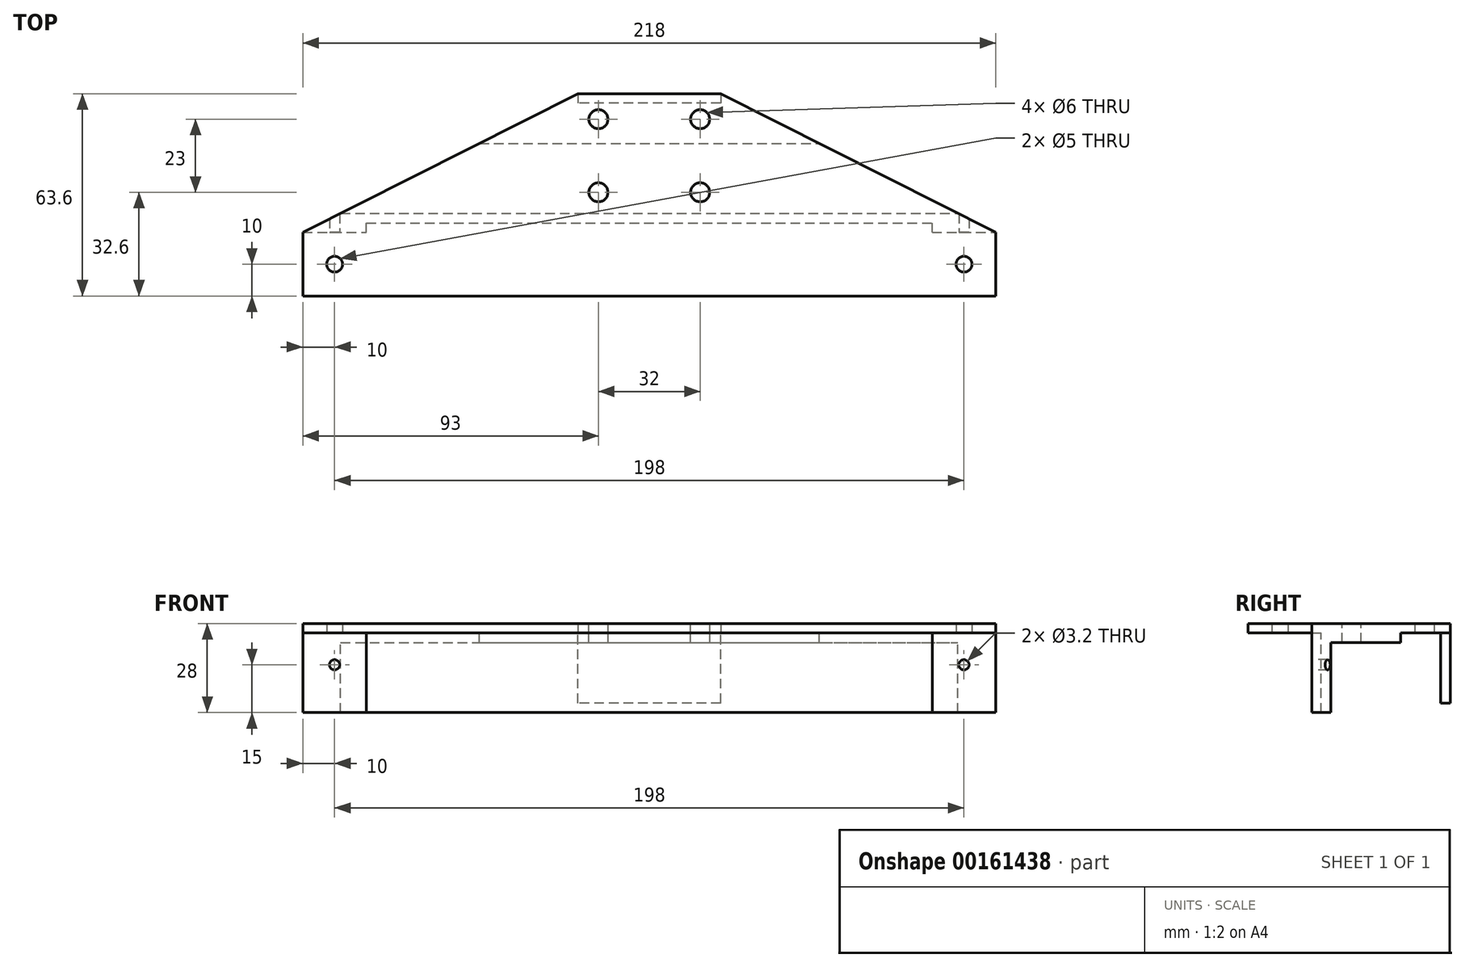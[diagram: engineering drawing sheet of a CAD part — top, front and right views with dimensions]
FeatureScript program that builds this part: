
annotation { "Feature Type Name" : "Feature", "Feature Type Description" : "" }
export const myFeature = defineFeature(function(context is Context, id is Id, definition is map)
    precondition{}
    {
        {
            var Q0;
            Q0=qCreatedBy(makeId("Top.planeOp"),FACE);
            var sketch = newSketch(context, id + "F0", { "sketchPlane" : qUnion([Q0])});
            skLineSegment(sketch, "E0.top", {"start": v(109, -10) * mm, "end": v(-109, -10) * mm});
            skLineSegment(sketch, "E0.left", {"start": v(109, 10) * mm, "end": v(109, -10) * mm});
            skLineSegment(sketch, "E0.right", {"start": v(-109, 10) * mm, "end": v(-109, -10) * mm});
            skLineSegment(sketch, "E1.bottom", {"start": v(22.5, 53.6) * mm, "end": v(-22.5, 53.6) * mm});
            skPoint(sketch, "E1.top.end.orphan", {"position": v(-22.5, -53.6) * mm});
            skPoint(sketch, "E1.top.start.orphan", {"position": v(22.5, -53.6) * mm});
            skLineSegment(sketch, "E2", {"start": v(-109, 10) * mm, "end": v(-22.5, 53.6) * mm});
            skLineSegment(sketch, "E3", {"start": v(22.5, 53.6) * mm, "end": v(109, 10) * mm});
            skPoint(sketch, "E4", {"position": v(-99, 0) * mm});
            skPoint(sketch, "E5", {"position": v(99, 0) * mm});
            skPoint(sketch, "E5.positionSnap0", {"position": v(109, 0) * mm});
            skCircle(sketch, "E6", {"center": v(-99, 0) * mm, "radius": 2.5 * mm});
            skCircle(sketch, "E7", {"center": v(99, 0) * mm, "radius": 2.5 * mm});
            skLineSegment(sketch, "E8.top", {"start": v(3, -10) * mm, "end": v(18, -10) * mm});
            skSolve(sketch);
        }
        {
            var Q0;
            Q0 = qSketchRegion(id + "F0", true);
            extrude(context, id + "F1", {"entities" : qUnion([Q0]), "depth" : 3 * mm});
        }
        {
            var Q0;
            Q0=makeQuery(id+"F1.opExtrude","CAP_FACE",FACE,{"disambiguationData":[OSD([sQuery(id+"F0.wireOp",EDGE,"E0.top"),sQuery(id+"F0.wireOp",EDGE,"E0.left"),sQuery(id+"F0.wireOp",EDGE,"E0.right"),sQuery(id+"F0.wireOp",EDGE,"E1.bottom"),sQuery(id+"F0.wireOp",EDGE,"E2"),sQuery(id+"F0.wireOp",EDGE,"E3"),sQuery(id+"F0.wireOp",EDGE,"E6"),sQuery(id+"F0.wireOp",EDGE,"E7")])],"isStart":true});
            var sketch = newSketch(context, id + "F2", { "sketchPlane" : qUnion([Q0])});
            skLineSegment(sketch, "E9.bottom", {"start": v(22.5, -53.6) * mm, "end": v(-22.5, -53.6) * mm});
            skLineSegment(sketch, "E9.top", {"start": v(22.5, -50.6) * mm, "end": v(-22.5, -50.6) * mm});
            skLineSegment(sketch, "E9.left", {"start": v(22.5, -53.6) * mm, "end": v(22.5, -50.6) * mm});
            skLineSegment(sketch, "E9.right", {"start": v(-22.5, -53.6) * mm, "end": v(-22.5, -50.6) * mm});
            skPoint(sketch, "E10.left.start.orphan", {"position": v(-89, 10) * mm});
            skPoint(sketch, "E10.right.start.orphan", {"position": v(89, 10) * mm});
            skSolve(sketch);
        }
        {
            var Q0;
            Q0 = qSketchRegion(id + "F2", true);
            extrude(context, id + "F3", {"entities" : qUnion([Q0]), "operationType" : NewBodyOperationType.ADD, "depth" : 22 * mm});
        }
        {
            var Q0;
            Q0=makeQuery(id+"F1.opExtrude","CAP_FACE",FACE,{"disambiguationData":[OSD([sQuery(id+"F0.wireOp",EDGE,"E0.top"),sQuery(id+"F0.wireOp",EDGE,"E0.left"),sQuery(id+"F0.wireOp",EDGE,"E0.right"),sQuery(id+"F0.wireOp",EDGE,"E1.bottom"),sQuery(id+"F0.wireOp",EDGE,"E2"),sQuery(id+"F0.wireOp",EDGE,"E3"),sQuery(id+"F0.wireOp",EDGE,"E6"),sQuery(id+"F0.wireOp",EDGE,"E7")])],"isStart":true});
            var sketch = newSketch(context, id + "F4", { "sketchPlane" : qUnion([Q0])});
            skPoint(sketch, "E11.right.end.orphan", {"position": v(109, -35) * mm});
            skLineSegment(sketch, "E12", {"start": v(-89, -13) * mm, "end": v(89, -13) * mm});
            skLineSegment(sketch, "E13", {"start": v(-53.45, -38) * mm, "end": v(53.45, -38) * mm});
            skLineSegment(sketch, "E14", {"start": v(-103.05, -13) * mm, "end": v(-53.45, -38) * mm});
            skLineSegment(sketch, "E15", {"start": v(53.45, -38) * mm, "end": v(103.05, -13) * mm});
            skLineSegment(sketch, "E16", {"start": v(-109, -10) * mm, "end": v(-89, -10) * mm});
            skLineSegment(sketch, "E17", {"start": v(-109, -10) * mm, "end": v(-103.05, -13) * mm});
            skLineSegment(sketch, "E18", {"start": v(109, -10) * mm, "end": v(103.05, -13) * mm});
            skLineSegment(sketch, "E19", {"start": v(89, -10) * mm, "end": v(89, -13) * mm});
            skLineSegment(sketch, "E20", {"start": v(-89, -10) * mm, "end": v(-89, -13) * mm});
            skLineSegment(sketch, "E21.trimOffspring", {"start": v(89, -10) * mm, "end": v(109, -10) * mm});
            skSolve(sketch);
        }
        {
            var Q0;
            Q0 = qSketchRegion(id + "F4", true);
            extrude(context, id + "F5", {"entities" : qUnion([Q0]), "operationType" : NewBodyOperationType.ADD, "depth" : 3 * mm});
        }
        {
            var Q0;
            Q0=makeQuery(id+"F5.opExtrude","CAP_FACE",FACE,{"disambiguationData":[OSD([sQuery(id+"F4.wireOp",EDGE,"E12"),sQuery(id+"F4.wireOp",EDGE,"E13"),sQuery(id+"F4.wireOp",EDGE,"E14"),sQuery(id+"F4.wireOp",EDGE,"E15"),sQuery(id+"F4.wireOp",EDGE,"E16"),sQuery(id+"F4.wireOp",EDGE,"E17"),sQuery(id+"F4.wireOp",EDGE,"E18"),sQuery(id+"F4.wireOp",EDGE,"E19"),sQuery(id+"F4.wireOp",EDGE,"E20"),sQuery(id+"F4.wireOp",EDGE,"E21.trimOffspring")])],"isStart":false});
            var sketch = newSketch(context, id + "F6", { "sketchPlane" : qUnion([Q0])});
            skLineSegment(sketch, "E22.bottom", {"start": v(-89, -13) * mm, "end": v(89, -13) * mm});
            skLineSegment(sketch, "E22.top", {"start": v(-97.1, -16) * mm, "end": v(97.1, -16) * mm});
            skLineSegment(sketch, "E23.bottom", {"start": v(-89, -10) * mm, "end": v(-109, -10) * mm});
            skLineSegment(sketch, "E23.left", {"start": v(-89, -10) * mm, "end": v(-89, -13) * mm});
            skLineSegment(sketch, "E24.bottom", {"start": v(89, -10) * mm, "end": v(109, -10) * mm});
            skLineSegment(sketch, "E24.left", {"start": v(89, -10) * mm, "end": v(89, -13) * mm});
            skPoint(sketch, "E23.right.end.orphan", {"position": v(-109, -13) * mm});
            skPoint(sketch, "E25.orphan", {"position": v(-103.05, -13) * mm});
            skPoint(sketch, "E24.right.end.orphan", {"position": v(109, -13) * mm});
            skLineSegment(sketch, "E26", {"start": v(-109, -10) * mm, "end": v(-97.1, -16) * mm});
            skLineSegment(sketch, "E27", {"start": v(109, -10) * mm, "end": v(97.1, -16) * mm});
            skSolve(sketch);
        }
        {
            var Q0;
            Q0=makeQuery(id+"F6.imprint","IMPRINT",FACE,{"disambiguationData":[TD([[makeQuery(id+"F6.imprint","IMPRINT",EDGE,{"derivedFrom":sQuery(id+"F6.wireOp",EDGE,"E22.bottom")}),-1.0]])]});
            extrude(context, id + "F7", {"entities" : qUnion([Q0]), "operationType" : NewBodyOperationType.ADD, "depth" : 22 * mm});
        }
        {
            var Q0;
            Q0=makeQuery(id+"F7.boolean.opBoolean","MERGE",FACE,{"derivedFrom":[makeQuery(id+"F5.opExtrude","SWEPT_FACE",FACE,{"disambiguationData":[OSD([sQuery(id+"F4.wireOp",EDGE,"E16")])]}),makeQuery(id+"F7.opExtrude","SWEPT_FACE",FACE,{"disambiguationData":[OSD([sQuery(id+"F6.wireOp",EDGE,"E23.bottom")])]})]});
            var sketch = newSketch(context, id + "F8", { "sketchPlane" : qUnion([Q0])});
            skCircle(sketch, "E28", {"center": v(-99, -10) * mm, "radius": 1.6 * mm});
            skCircle(sketch, "E29", {"center": v(99, -10) * mm, "radius": 1.6 * mm});
            skSolve(sketch);
        }
        {
            var Q0;
            Q0 = qSketchRegion(id + "F8", true);
            extrude(context, id + "F9", {"entities" : qUnion([Q0]), "operationType" : NewBodyOperationType.REMOVE, "oppositeDirection" : true, "depth" : 6 * mm});
        }
        {
            var Q0;
            Q0=makeQuery(id+"F1.opExtrude","CAP_FACE",FACE,{"disambiguationData":[OSD([sQuery(id+"F0.wireOp",EDGE,"E0.top"),sQuery(id+"F0.wireOp",EDGE,"E0.left"),sQuery(id+"F0.wireOp",EDGE,"E0.right"),sQuery(id+"F0.wireOp",EDGE,"E1.bottom"),sQuery(id+"F0.wireOp",EDGE,"E2"),sQuery(id+"F0.wireOp",EDGE,"E3"),sQuery(id+"F0.wireOp",EDGE,"E6"),sQuery(id+"F0.wireOp",EDGE,"E7"),sQuery(id+"F0.wireOp",EDGE,"E8.top")])],"isStart":false});
            var sketch = newSketch(context, id + "F10", { "sketchPlane" : qUnion([Q0])});
            skCircle(sketch, "E30", {"center": v(-16, 45.6) * mm, "radius": 3 * mm});
            skCircle(sketch, "E31", {"center": v(-16, 22.6) * mm, "radius": 3 * mm});
            skCircle(sketch, "E32", {"center": v(16, 22.6) * mm, "radius": 3 * mm});
            skCircle(sketch, "E33", {"center": v(16, 45.6) * mm, "radius": 3 * mm});
            skSolve(sketch);
        }
        {
            var Q0;
            Q0 = qSketchRegion(id + "F10", true);
            extrude(context, id + "F11", {"entities" : qUnion([Q0]), "operationType" : NewBodyOperationType.REMOVE, "oppositeDirection" : true, "depth" : 25 * mm});
        }
        {
            var Q0;
            Q0 = qSketchRegion(id + "F10", true);
            extrude(context, id + "F12", {"entities" : qUnion([Q0]), "operationType" : NewBodyOperationType.REMOVE, "oppositeDirection" : true, "depth" : 30 * mm});
        }
    });
